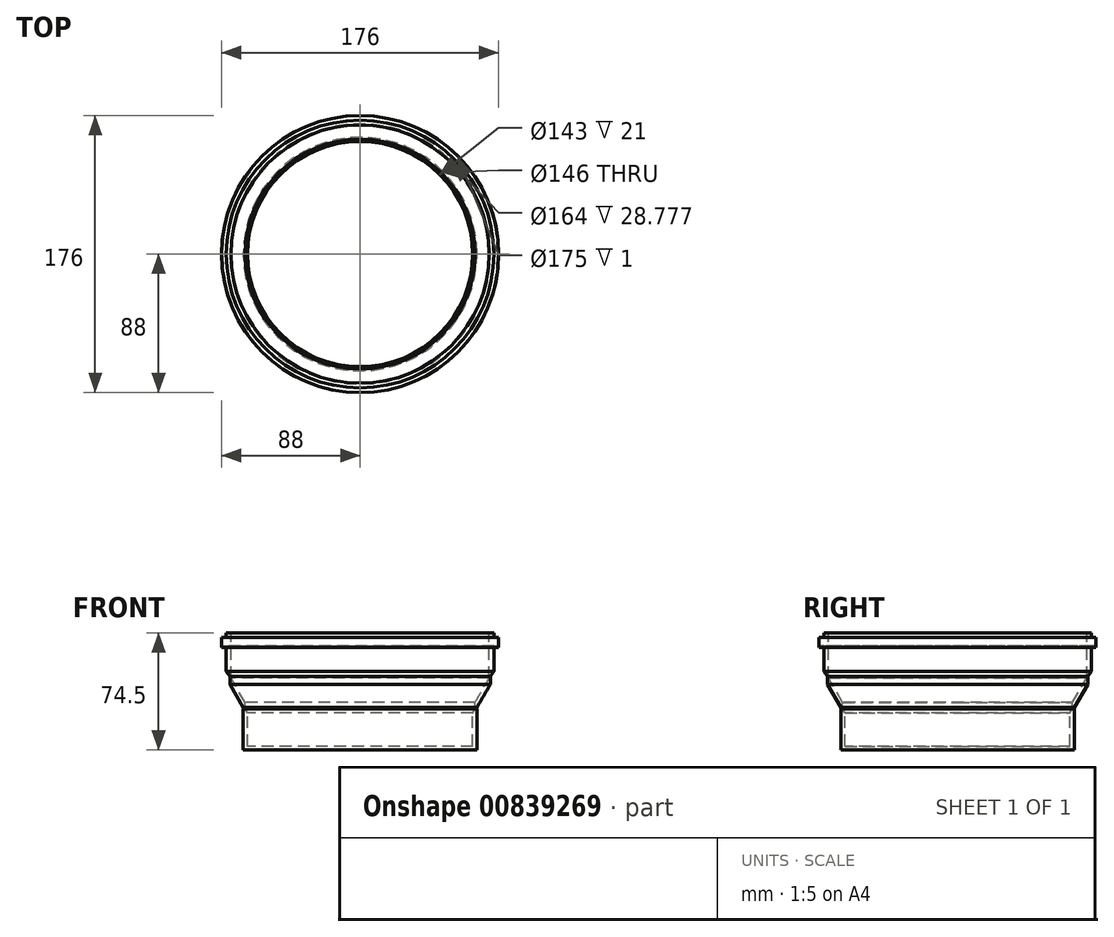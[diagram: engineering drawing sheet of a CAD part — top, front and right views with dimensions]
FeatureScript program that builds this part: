
annotation { "Feature Type Name" : "Feature", "Feature Type Description" : "" }
export const myFeature = defineFeature(function(context is Context, id is Id, definition is map)
    precondition{}
    {
        {
            var Q0;
            Q0=qCreatedBy(makeId("Front.planeOp"),FACE);
            var sketch = newSketch(context, id + "F0", { "sketchPlane" : qUnion([Q0])});
            skLineSegment(sketch, "E0", {"start": v(-82, 63) * mm, "end": v(-85, 63) * mm});
            skLineSegment(sketch, "E1", {"start": v(-85, 63) * mm, "end": v(-85, 48) * mm});
            skLineSegment(sketch, "E2", {"start": v(-85, 48) * mm, "end": v(-82.7, 44.72) * mm});
            skLineSegment(sketch, "E3", {"start": v(-82.7, 44.72) * mm, "end": v(-82.7, 43.72) * mm});
            skLineSegment(sketch, "E4", {"start": v(-82.7, 43.72) * mm, "end": v(-82.7, 39.72) * mm});
            skLineSegment(sketch, "E5", {"start": v(-82.7, 39.72) * mm, "end": v(-74.2, 25) * mm});
            skLineSegment(sketch, "E6", {"start": v(-74.2, 25) * mm, "end": v(-74, 25) * mm});
            skLineSegment(sketch, "E7", {"start": v(-74, 25) * mm, "end": v(-74, 24) * mm});
            skLineSegment(sketch, "E8", {"start": v(-82, 63) * mm, "end": v(-82, 43.72) * mm});
            skLineSegment(sketch, "E9", {"start": v(-82, 43.72) * mm, "end": v(-73, 28.13) * mm});
            skLineSegment(sketch, "E10", {"start": v(-73, 28.13) * mm, "end": v(-73, 24) * mm});
            skLineSegment(sketch, "E11", {"start": v(-74, 24) * mm, "end": v(-74.2, 24) * mm});
            skLineSegment(sketch, "E12", {"start": v(-73, 24) * mm, "end": v(-71.5, 21.4) * mm});
            skLineSegment(sketch, "E13", {"start": v(-74.2, 24) * mm, "end": v(-74.2, -2) * mm});
            skLineSegment(sketch, "E14", {"start": v(-71.5, 21.4) * mm, "end": v(-71.5, 0.4) * mm});
            skLineSegment(sketch, "E15", {"start": v(-74.2, -2) * mm, "end": v(0, -2) * mm});
            skLineSegment(sketch, "E16", {"start": v(-71.5, 0.4) * mm, "end": v(0, 0.4) * mm});
            skLineSegment(sketch, "E17", {"start": v(0, 0.4) * mm, "end": v(0, -2) * mm});
            skPoint(sketch, "E18.orphan", {"position": v(0, 63) * mm});
            skLineSegment(sketch, "E19", {"start": v(0, 79.75) * mm, "end": v(0, -22.5) * mm, "construction": true});
            skSolve(sketch);
        }
        {
            var Q0;
            Q0 = qSketchRegion(id + "F0", true);
            var Q1;
            Q1=sQuery(id+"F0.wireOp",EDGE,"E19");
            revolve(context, id + "F1", {"surfaceOperationType" : NewSurfaceOperationType.NEW, "entities" : qUnion([Q0]), "axis" : qUnion([Q1]), "revolveType" : RevolveType.FULL});
        }
        {
            var Q0;
            Q0=qCreatedBy(makeId("Front.planeOp"),FACE);
            var sketch = newSketch(context, id + "F2", { "sketchPlane" : qUnion([Q0])});
            skLineSegment(sketch, "E20", {"start": v(0, 63) * mm, "end": v(0, 98.43) * mm, "construction": true});
            skLineSegment(sketch, "E21", {"start": v(-88, 63) * mm, "end": v(-88, 69.5) * mm});
            skLineSegment(sketch, "E22", {"start": v(-88, 69.5) * mm, "end": v(-82, 69.5) * mm});
            skLineSegment(sketch, "E23", {"start": v(-82, 69.5) * mm, "end": v(-82, 63) * mm});
            skLineSegment(sketch, "E24.trimOffspring", {"start": v(0, 63) * mm, "end": v(85, 63) * mm, "construction": true});
            skPoint(sketch, "E25.end.orphan", {"position": v(-85, 63) * mm});
            skLineSegment(sketch, "E26", {"start": v(-88, 63) * mm, "end": v(-82, 63) * mm});
            skSolve(sketch);
        }
        {
            var Q0;
            Q0 = qSketchRegion(id + "F2", true);
            var Q1;
            Q1=sQuery(id+"F2.wireOp",EDGE,"E20");
            revolve(context, id + "F3", {"operationType" : NewBodyOperationType.ADD, "surfaceOperationType" : NewSurfaceOperationType.NEW, "entities" : qUnion([Q0]), "axis" : qUnion([Q1]), "revolveType" : RevolveType.FULL});
        }
        {
            var Q0;
            Q0=makeQuery(id+"F3.opRevolve","SWEPT_FACE",FACE,{"disambiguationData":[OSD([sQuery(id+"F2.wireOp",EDGE,"E22")])]});
            var sketch = newSketch(context, id + "F4", { "sketchPlane" : qUnion([Q0])});
            skCircle(sketch, "E27.0", {"center": v(0, 0) * mm, "radius": 82 * mm});
            skCircle(sketch, "E28.0", {"center": v(0, 0) * mm, "radius": 85 * mm});
            skSolve(sketch);
        }
        {
            var Q0;
            Q0=makeQuery(id+"F4.imprint","IMPRINT",FACE,{"disambiguationData":[TD([[makeQuery(id+"F4.imprint","IMPRINT",EDGE,{"derivedFrom":sQuery(id+"F4.wireOp",EDGE,"E27.0")}),1.0]])]});
            extrude(context, id + "F5", {"entities" : qUnion([Q0]), "operationType" : NewBodyOperationType.ADD, "depth" : 3 * mm, "offsetDistance" : 25 * mm});
        }
        {
            var Q0;
            Q0=makeQuery(id+"F3.opRevolve","SWEPT_FACE",FACE,{"disambiguationData":[OSD([sQuery(id+"F2.wireOp",EDGE,"E26")])]});
            var sketch = newSketch(context, id + "F6", { "sketchPlane" : qUnion([Q0])});
            skCircle(sketch, "E29", {"center": v(0, 0) * mm, "radius": 87.5 * mm});
            skCircle(sketch, "E30.0", {"center": v(0, 0) * mm, "radius": 85 * mm});
            skSolve(sketch);
        }
        {
            var Q0;
            Q0 = qSketchRegion(id + "F6", true);
            extrude(context, id + "F7", {"entities" : qUnion([Q0]), "operationType" : NewBodyOperationType.REMOVE, "oppositeDirection" : true, "depth" : 1 * mm, "offsetDistance" : 25 * mm});
        }
    });
